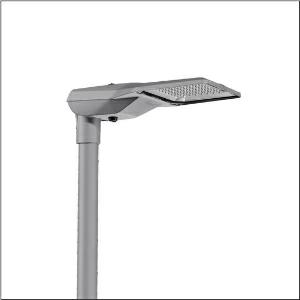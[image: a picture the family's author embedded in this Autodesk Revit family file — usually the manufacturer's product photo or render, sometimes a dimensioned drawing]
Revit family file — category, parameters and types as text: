
# Revit family: streetlight_sl_21_midi___st0_8a_5xe3c33t08lb_3015
name_source: partatom
category: Lighting Fixtures
units: mm (PartAtom-declared; Revit-internal decimal feet)

## family parameters
Cut with Voids When Loaded = No
Host = Face
Light Source = No
Part Type = Normal
Room Calculation Point = No
Round Connector Dimension = Use Diameter
Shared = No

## types (1)
- --- (1 x LED, 14340 lm, 98.3 W, 3000K)
    Apparent Load = 98 VA
    CIE Flux Codes = 38 75 97 100 100
    Color Rendering = 70
    Color Temperature = 3000K
    Default Elevation = 1800 mm
    Description = Streetlight SL 21 midi, mast luminaire, primary light control with lens, of PMMA, primary optical cover: cover, of toughened safety glass, transparent, light distribution: ST0.8a, light emission: direct distribution, primary light characteristic: asymmetric, installation type: side-entry, post-top, LED, High Power LED, rated luminous flux: 14.340lm, luminous efficacy: 146lm/W, light colour: 730, colour temperature: 3000K, control: overheat protection, constant luminous flux control, time-dependent luminous flux control, flexible luminous flux parameterisation, presetting dimming logarithmic, mains connection: 230..240V, AC, 50/60Hz, start of lifetime: 98W, end of service life: 101W, reduction: 45W, luminaire housing, of diecast aluminium, powder-coated, Siteco® metallic grey (DB 702S), corrosivity category C5 mid according to DIN EN ISO 12944, please order mast flange separately, inclination adjustable: 0°, 5°, 10°, 15°, sealing non-destructively replaceable, multi-level sealing system, length: 644mm, width: 335mm, height: 110mm, mast flange for spigot size: 42mm (side-entry): 5XC10008XM4, 60/48mm (side-entry/post-top): 5XC10108XM2, 76/60mm (side-entry/post-top): 5XC10108XM1, Smart Interface below and above, protection rating (complete): IP66, insulation class (complete): insulation class II (safety insulation), certification: CE, ENEC, ENEC+, VDE, impact resistance: IK09, permissible operating ambient temperature for outdoor applications: -40..+50°C, standard-compliant lighting for roads and squares, packaging unit: 1 piece

Light Distribution: ST0.8a
    Height = 111 mm
    Lamp = 1 x LED
    Lamp Light Flux = 14340 lm
    Lamp Power = 98.3 W
    Lamp count = 1
    Length = 644 mm
    Luminous efficacy = 146 lm/W
    Manufacturer = Siteco
    ModVariant = No
    Model = 5XE3C33T08LB
    Number of Poles = 1
    OnlyDefault = Yes
    Power Factor = 1
    Product Name = Streetlight SL 21 midi | ST0.8a
    Product group = mast luminaire | pylon top
    ProductGroupID = 6100
    Protection Class = Protection class II
    Protection Degree = IP 66
    RLX_Detail_Level = 1
    RLX_Emergency_Light_Flux = 0 lm
    RLX_Emergency_Type = 0
    RLX_Emergency_Type_DB = No
    RlxData = <blob elided: 90985 chars, md5=9f53ce25>
    Socket = socket
    Standby Power = 0 W
    System Light Flux = 14340 lm
    System Power = 98 W
    Type Comments = factory setting: luminous flux: 100 % | dim-lin: 254 | 1020 mA
    Type Image = l_1004304.jpg
    URL = http://relux.com
    VarID = @adj_137745
    Voltage = 0 V
    Weight = 0.00 kg
    Width = 336 mm

## geometry (parser evidence)
native form markers: Blend x4, Sweep x10
no freeform markers — native parametric forms only
